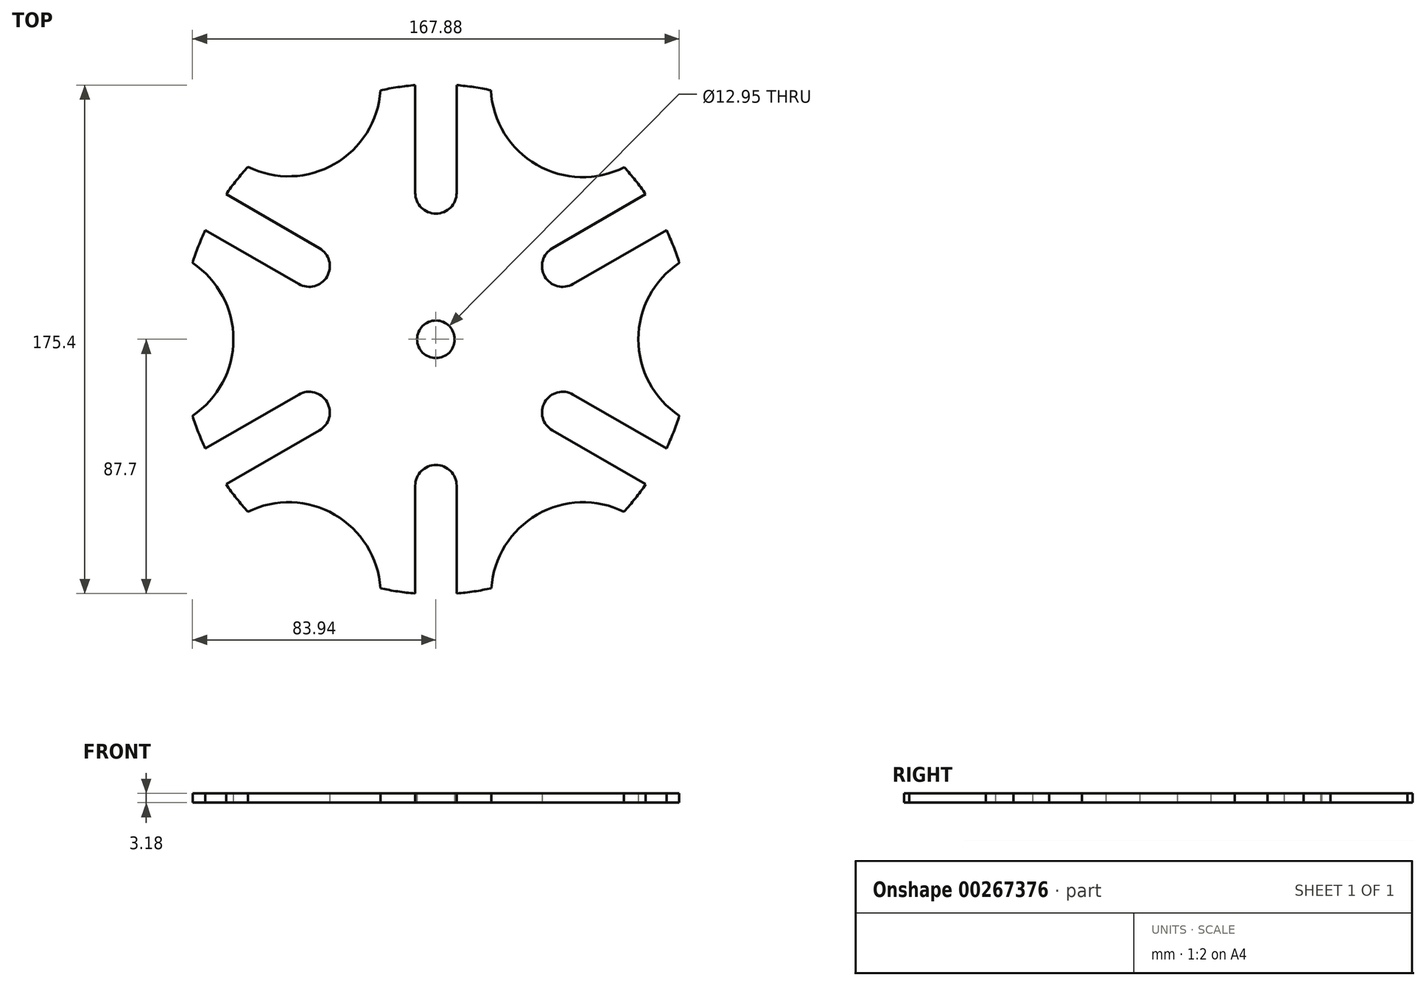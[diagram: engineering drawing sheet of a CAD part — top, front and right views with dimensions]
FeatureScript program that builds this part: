
annotation { "Feature Type Name" : "Feature", "Feature Type Description" : "" }
export const myFeature = defineFeature(function(context is Context, id is Id, definition is map)
    precondition{}
    {
        {
            var Q0;
            Q0=qCreatedBy(makeId("Top.planeOp"),FACE);
            var sketch = newSketch(context, id + "F0", { "sketchPlane" : qUnion([Q0])});
            skArc(sketch, "E0", {"start": v(18.93, 85.93) * mm, "mid": v(13.07, 87.01) * mm, "end": v(7.14, 87.7) * mm});
            skLineSegment(sketch, "E1", {"start": v(0, 6.48) * mm, "end": v(0, 43.37) * mm});
            skLineSegment(sketch, "E2", {"start": v(5.6, 3.24) * mm, "end": v(37.56, 21.68) * mm});
            skLineSegment(sketch, "E3", {"start": v(5.6, -3.24) * mm, "end": v(37.56, -21.68) * mm});
            skLineSegment(sketch, "E4", {"start": v(0, -6.48) * mm, "end": v(0, -43.37) * mm});
            skLineSegment(sketch, "E5", {"start": v(-5.6, -3.24) * mm, "end": v(-37.56, -21.68) * mm});
            skLineSegment(sketch, "E6", {"start": v(-5.6, 3.24) * mm, "end": v(-37.56, 21.68) * mm});
            skLineSegment(sketch, "E7", {"start": v(7.14, 50.5) * mm, "end": v(7.14, 87.7) * mm});
            skLineSegment(sketch, "E8", {"start": v(-7.14, 50.5) * mm, "end": v(-7.14, 87.7) * mm});
            skLineSegment(sketch, "E9", {"start": v(72.38, 50.04) * mm, "end": v(40.17, 31.44) * mm});
            skLineSegment(sketch, "E10", {"start": v(47.31, 19.07) * mm, "end": v(79.52, 37.66) * mm});
            skLineSegment(sketch, "E11", {"start": v(72.38, -50.04) * mm, "end": v(40.17, -31.44) * mm});
            skLineSegment(sketch, "E12", {"start": v(47.31, -19.07) * mm, "end": v(79.52, -37.66) * mm});
            skLineSegment(sketch, "E13", {"start": v(-7.14, -87.7) * mm, "end": v(-7.14, -50.5) * mm});
            skLineSegment(sketch, "E14", {"start": v(7.14, -50.5) * mm, "end": v(7.14, -87.7) * mm});
            skLineSegment(sketch, "E15", {"start": v(-79.52, -37.66) * mm, "end": v(-47.31, -19.07) * mm});
            skLineSegment(sketch, "E16", {"start": v(-40.17, -31.44) * mm, "end": v(-72.38, -50.04) * mm});
            skArc(sketch, "E17", {"start": v(-7.14, 50.5) * mm, "mid": v(0, 43.37) * mm, "end": v(7.14, 50.5) * mm});
            skArc(sketch, "E18", {"start": v(40.17, 31.44) * mm, "mid": v(37.56, 21.68) * mm, "end": v(47.31, 19.07) * mm});
            skArc(sketch, "E19", {"start": v(47.31, -19.07) * mm, "mid": v(37.56, -21.68) * mm, "end": v(40.17, -31.44) * mm});
            skArc(sketch, "E20", {"start": v(7.14, -50.5) * mm, "mid": v(0, -43.37) * mm, "end": v(-7.14, -50.5) * mm});
            skArc(sketch, "E21", {"start": v(-40.17, -31.44) * mm, "mid": v(-37.56, -21.68) * mm, "end": v(-47.31, -19.07) * mm});
            skLineSegment(sketch, "E22", {"start": v(-40.17, 31.44) * mm, "end": v(-72.38, 50.04) * mm});
            skLineSegment(sketch, "E23", {"start": v(-79.52, 37.66) * mm, "end": v(-47.31, 19.07) * mm});
            skArc(sketch, "E24", {"start": v(-47.31, 19.07) * mm, "mid": v(-37.56, 21.68) * mm, "end": v(-40.17, 31.44) * mm});
            skLineSegment(sketch, "E25", {"start": v(3.24, 5.6) * mm, "end": v(34.76, 60.2) * mm});
            skLineSegment(sketch, "E26", {"start": v(6.48, 0) * mm, "end": v(69.85, 0) * mm});
            skLineSegment(sketch, "E27", {"start": v(3.24, -5.6) * mm, "end": v(34.92, -60.5) * mm});
            skLineSegment(sketch, "E28", {"start": v(-3.24, -5.6) * mm, "end": v(-34.92, -60.5) * mm});
            skLineSegment(sketch, "E29", {"start": v(-6.48, 0) * mm, "end": v(-69.85, 0) * mm});
            skLineSegment(sketch, "E30", {"start": v(-3.24, 5.6) * mm, "end": v(-34.92, 60.5) * mm});
            skArc(sketch, "E31", {"start": v(64.95, 59.36) * mm, "mid": v(34.76, 60.2) * mm, "end": v(18.93, 85.93) * mm});
            skPoint(sketch, "E32.startSnap0", {"position": v(88.9, 22) * mm});
            skArc(sketch, "E33", {"start": v(64.82, -59.5) * mm, "mid": v(34.92, -60.5) * mm, "end": v(19.12, -85.89) * mm});
            skArc(sketch, "E34", {"start": v(-19.12, -85.89) * mm, "mid": v(-34.92, -60.5) * mm, "end": v(-64.82, -59.5) * mm});
            skArc(sketch, "E35", {"start": v(-83.94, -26.38) * mm, "mid": v(-69.85, 0) * mm, "end": v(-83.94, 26.38) * mm});
            skArc(sketch, "E36", {"start": v(-64.82, 59.5) * mm, "mid": v(-34.92, 60.5) * mm, "end": v(-19.12, 85.89) * mm});
            skArc(sketch, "E37", {"start": v(83.94, 26.38) * mm, "mid": v(69.85, 0) * mm, "end": v(83.94, -26.38) * mm});
            skCircle(sketch, "E38", {"center": v(0, 0) * mm, "radius": 6.48 * mm});
            skArc(sketch, "E39.trimOffspring", {"start": v(83.94, 26.38) * mm, "mid": v(81.92, 32.1) * mm, "end": v(79.52, 37.66) * mm});
            skArc(sketch, "E40.trimOffspring", {"start": v(64.82, -59.5) * mm, "mid": v(68.76, -54.9) * mm, "end": v(72.38, -50.04) * mm});
            skArc(sketch, "E41.trimOffspring", {"start": v(-19.12, -85.89) * mm, "mid": v(-13.16, -87) * mm, "end": v(-7.14, -87.7) * mm});
            skArc(sketch, "E42.trimOffspring", {"start": v(-83.94, -26.38) * mm, "mid": v(-81.92, -32.1) * mm, "end": v(-79.52, -37.66) * mm});
            skArc(sketch, "E43.trimOffspring", {"start": v(-64.82, 59.5) * mm, "mid": v(-68.76, 54.9) * mm, "end": v(-72.38, 50.04) * mm});
            skArc(sketch, "E44.trimOffspring", {"start": v(-7.14, 87.7) * mm, "mid": v(-13.16, 87) * mm, "end": v(-19.12, 85.89) * mm});
            skPoint(sketch, "E45.orphan", {"position": v(76.2, 44) * mm});
            skArc(sketch, "E46.trimOffspring", {"start": v(72.38, 50.04) * mm, "mid": v(68.82, 54.82) * mm, "end": v(64.95, 59.36) * mm});
            skArc(sketch, "E47.trimOffspring", {"start": v(79.52, -37.66) * mm, "mid": v(81.92, -32.1) * mm, "end": v(83.94, -26.38) * mm});
            skArc(sketch, "E48.trimOffspring", {"start": v(7.14, -87.7) * mm, "mid": v(13.16, -87) * mm, "end": v(19.12, -85.89) * mm});
            skArc(sketch, "E49.trimOffspring", {"start": v(-72.38, -50.04) * mm, "mid": v(-68.76, -54.9) * mm, "end": v(-64.82, -59.5) * mm});
            skArc(sketch, "E50.trimOffspring", {"start": v(-79.52, 37.66) * mm, "mid": v(-81.92, 32.1) * mm, "end": v(-83.94, 26.38) * mm});
            skLineSegment(sketch, "E51", {"start": v(-5.6, 3.24) * mm, "end": v(-76.2, 44) * mm});
            skSolve(sketch);
        }
        {
            var Q0;
            {var subQ2=sQuery(id+"F0.wireOp",EDGE,"E1");Q0=makeQuery(id+"F0.imprint","IMPRINT",FACE,{"disambiguationData":[TD([[makeQuery(id+"F0.imprint","IMPRINT",EDGE,{"derivedFrom":subQ2}),1.0]])]});}
            var Q1;
            {var subQ1=sQuery(id+"F0.wireOp",EDGE,"E6");Q1=makeQuery(id+"F0.imprint","IMPRINT",FACE,{"disambiguationData":[TD([[makeQuery(id+"F0.imprint","IMPRINT",EDGE,{"derivedFrom":subQ1}),-1.0]])]});}
            var Q2;
            {var subQ1=sQuery(id+"F0.wireOp",EDGE,"E6");Q2=makeQuery(id+"F0.imprint","IMPRINT",FACE,{"disambiguationData":[TD([[makeQuery(id+"F0.imprint","IMPRINT",EDGE,{"derivedFrom":subQ1}),1.0]])]});}
            var Q3;
            {var subQ1=sQuery(id+"F0.wireOp",EDGE,"E5");Q3=makeQuery(id+"F0.imprint","IMPRINT",FACE,{"disambiguationData":[TD([[makeQuery(id+"F0.imprint","IMPRINT",EDGE,{"derivedFrom":subQ1}),-1.0]])]});}
            var Q4;
            {var subQ1=sQuery(id+"F0.wireOp",EDGE,"E5");Q4=makeQuery(id+"F0.imprint","IMPRINT",FACE,{"disambiguationData":[TD([[makeQuery(id+"F0.imprint","IMPRINT",EDGE,{"derivedFrom":subQ1}),1.0]])]});}
            var Q5;
            {var subQ1=sQuery(id+"F0.wireOp",EDGE,"E4");Q5=makeQuery(id+"F0.imprint","IMPRINT",FACE,{"disambiguationData":[TD([[makeQuery(id+"F0.imprint","IMPRINT",EDGE,{"derivedFrom":subQ1}),-1.0]])]});}
            var Q6;
            {var subQ2=sQuery(id+"F0.wireOp",EDGE,"E4");Q6=makeQuery(id+"F0.imprint","IMPRINT",FACE,{"disambiguationData":[TD([[makeQuery(id+"F0.imprint","IMPRINT",EDGE,{"derivedFrom":subQ2}),1.0]])]});}
            var Q7;
            {var subQ1=sQuery(id+"F0.wireOp",EDGE,"E3");Q7=makeQuery(id+"F0.imprint","IMPRINT",FACE,{"disambiguationData":[TD([[makeQuery(id+"F0.imprint","IMPRINT",EDGE,{"derivedFrom":subQ1}),-1.0]])]});}
            var Q8;
            {var subQ1=sQuery(id+"F0.wireOp",EDGE,"E3");Q8=makeQuery(id+"F0.imprint","IMPRINT",FACE,{"disambiguationData":[TD([[makeQuery(id+"F0.imprint","IMPRINT",EDGE,{"derivedFrom":subQ1}),1.0]])]});}
            var Q9;
            {var subQ1=sQuery(id+"F0.wireOp",EDGE,"E2");Q9=makeQuery(id+"F0.imprint","IMPRINT",FACE,{"disambiguationData":[TD([[makeQuery(id+"F0.imprint","IMPRINT",EDGE,{"derivedFrom":subQ1}),-1.0]])]});}
            var Q10;
            {var subQ4=sQuery(id+"F0.wireOp",EDGE,"E2");Q10=makeQuery(id+"F0.imprint","IMPRINT",FACE,{"disambiguationData":[TD([[makeQuery(id+"F0.imprint","IMPRINT",EDGE,{"derivedFrom":subQ4}),1.0]])]});}
            var Q11;
            {var subQ3=sQuery(id+"F0.wireOp",EDGE,"E0");Q11=makeQuery(id+"F0.imprint","IMPRINT",FACE,{"disambiguationData":[TD([[makeQuery(id+"F0.imprint","IMPRINT",EDGE,{"derivedFrom":subQ3}),1.0]])]});}
            var Q12;
            {var subQ3=sQuery(id+"F0.wireOp",EDGE,"E1");Q12=makeQuery(id+"F0.imprint","IMPRINT",FACE,{"disambiguationData":[TD([[makeQuery(id+"F0.imprint","IMPRINT",EDGE,{"derivedFrom":subQ3}),-1.0]])]});}
            var Q13;
            {var subQ4=sQuery(id+"F0.wireOp",EDGE,"E22");Q13=makeQuery(id+"F0.imprint","IMPRINT",FACE,{"disambiguationData":[TD([[makeQuery(id+"F0.imprint","IMPRINT",EDGE,{"derivedFrom":subQ4}),-1.0]])]});}
            var Q14;
            {var subQ8=sQuery(id+"F0.wireOp",EDGE,"E23");Q14=makeQuery(id+"F0.imprint","IMPRINT",FACE,{"disambiguationData":[TD([[makeQuery(id+"F0.imprint","IMPRINT",EDGE,{"derivedFrom":subQ8}),-1.0]])]});}
            extrude(context, id + "F1", {"entities" : qUnion([Q0, Q1, Q2, Q3, Q4, Q5, Q6, Q7, Q8, Q9, Q10, Q11, Q12, Q13, Q14]), "depth" : 3.17 * mm});
        }
    });
